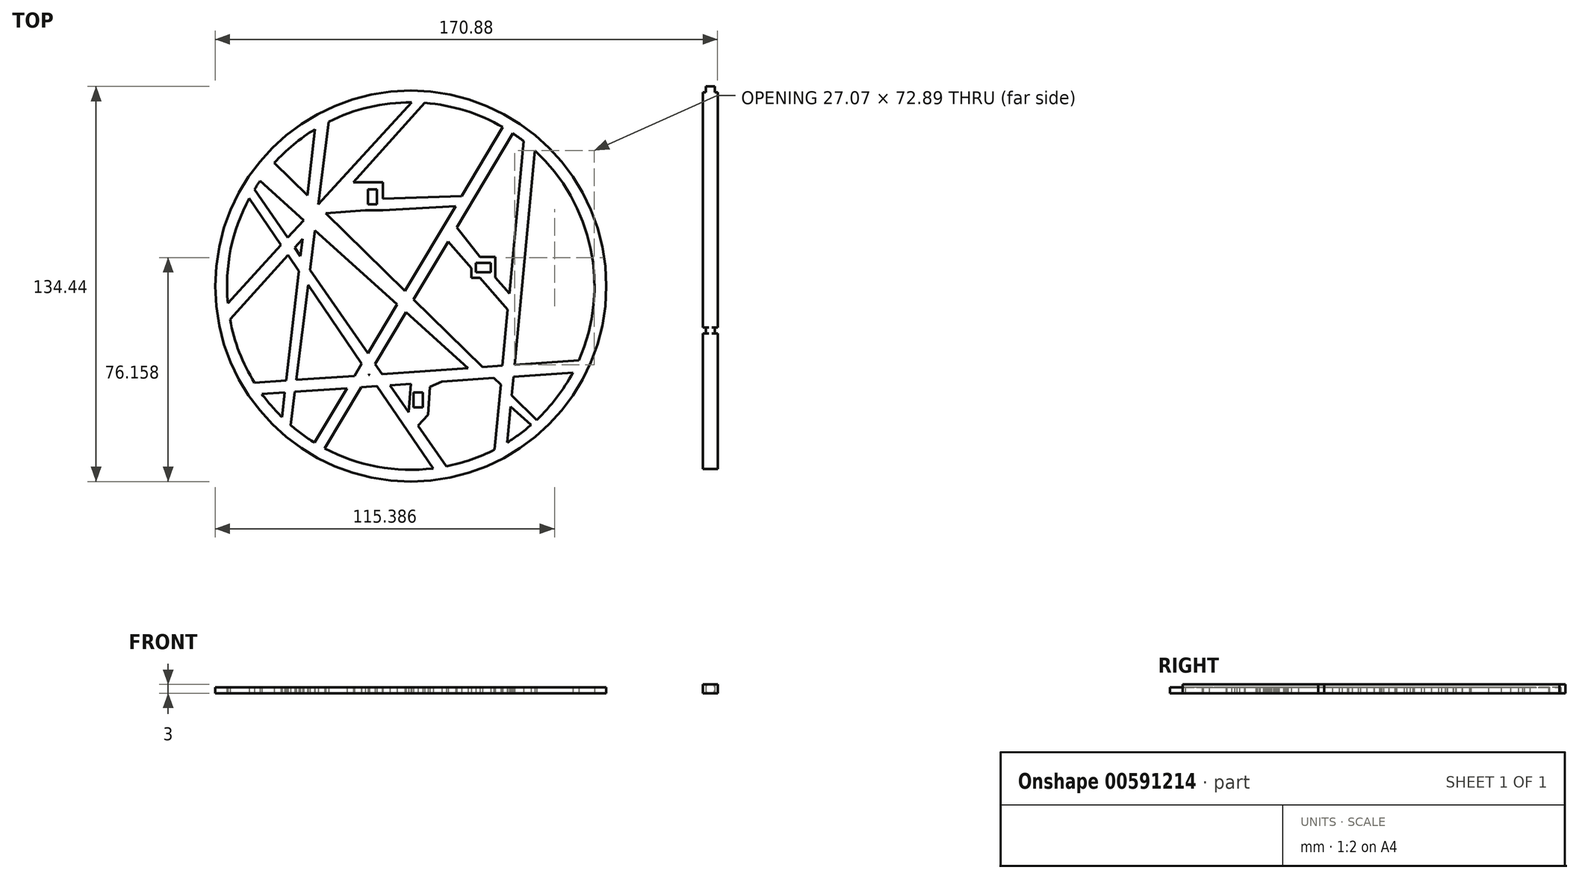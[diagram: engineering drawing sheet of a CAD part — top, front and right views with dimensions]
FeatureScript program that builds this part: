
annotation { "Feature Type Name" : "Feature", "Feature Type Description" : "" }
export const myFeature = defineFeature(function(context is Context, id is Id, definition is map)
    precondition{}
    {
        {
            var Q0;
            Q0=qCreatedBy(makeId("Top.planeOp"),FACE);
            var sketch = newSketch(context, id + "F0", { "sketchPlane" : qUnion([Q0])});
            skCircle(sketch, "E0", {"center": v(0, 0) * mm, "radius": 66.5 * mm});
            skArc(sketch, "E1.0", {"start": v(38.38, 49.32) * mm, "mid": v(36.59, 50.67) * mm, "end": v(34.75, 51.95) * mm});
            skLineSegment(sketch, "E2", {"start": v(-54.93, 29.82) * mm, "end": v(-44.14, 13.98) * mm});
            skLineSegment(sketch, "E3", {"start": v(-53.14, -32.9) * mm, "end": v(-42.35, -32.16) * mm});
            skLineSegment(sketch, "E4", {"start": v(-32.73, -53.24) * mm, "end": v(-21.68, -34.74) * mm});
            skLineSegment(sketch, "E5.0", {"start": v(-29.26, -55.23) * mm, "end": v(-16.82, -34.4) * mm});
            skLineSegment(sketch, "E6.0", {"start": v(32.88, -53.15) * mm, "end": v(34.02, -41.03) * mm});
            skLineSegment(sketch, "E7.0", {"start": v(-50.56, -36.74) * mm, "end": v(-42.82, -36.2) * mm});
            skLineSegment(sketch, "E8.trimOffspring", {"start": v(45.68, -48.33) * mm, "end": v(34.37, -37.25) * mm});
            skLineSegment(sketch, "E9.trimOffspring", {"start": v(40.92, -47.25) * mm, "end": v(34.02, -41.03) * mm});
            skLineSegment(sketch, "E10.trimOffspring", {"start": v(28.53, -55.6) * mm, "end": v(30.6, -33.56) * mm});
            skLineSegment(sketch, "E11.trimOffspring", {"start": v(-53.17, 32.85) * mm, "end": v(-41.84, 16.49) * mm});
            skLineSegment(sketch, "E12.trimOffspring", {"start": v(-32.53, 53.37) * mm, "end": v(-35.12, 30.81) * mm});
            skLineSegment(sketch, "E13.trimOffspring", {"start": v(-27.92, 55.92) * mm, "end": v(-31.43, 27.86) * mm});
            skLineSegment(sketch, "E14.trimOffspring", {"start": v(0.28, 62.5) * mm, "end": v(-31.43, 27.86) * mm});
            skArc(sketch, "E15.trimOffspring", {"start": v(31.35, 54.07) * mm, "mid": v(18.54, 59.69) * mm, "end": v(4.8, 62.32) * mm});
            skLineSegment(sketch, "E16.trimOffspring", {"start": v(4.8, 62.32) * mm, "end": v(-19.45, 35.37) * mm});
            skArc(sketch, "E17.trimOffspring", {"start": v(0.28, 62.5) * mm, "mid": v(-14.2, 60.86) * mm, "end": v(-27.92, 55.92) * mm});
            skArc(sketch, "E18.trimOffspring", {"start": v(-32.53, 53.37) * mm, "mid": v(-39.88, 48.12) * mm, "end": v(-46.4, 41.87) * mm});
            skArc(sketch, "E19.trimOffspring", {"start": v(-51.24, 35.8) * mm, "mid": v(-52.23, 34.33) * mm, "end": v(-53.17, 32.85) * mm});
            skArc(sketch, "E20.trimOffspring", {"start": v(-54.93, 29.82) * mm, "mid": v(-61.23, 12.56) * mm, "end": v(-62.23, -5.79) * mm});
            skArc(sketch, "E21.trimOffspring", {"start": v(-61.47, -11.32) * mm, "mid": v(-58.3, -22.5) * mm, "end": v(-53.14, -32.9) * mm});
            skArc(sketch, "E22.trimOffspring", {"start": v(-50.56, -36.74) * mm, "mid": v(-47.34, -40.81) * mm, "end": v(-43.78, -44.6) * mm});
            skLineSegment(sketch, "E23.trimOffspring", {"start": v(-42.82, -36.2) * mm, "end": v(-43.78, -44.6) * mm});
            skLineSegment(sketch, "E24.trimOffspring", {"start": v(-39.42, -35.97) * mm, "end": v(-40.84, -47.31) * mm});
            skLineSegment(sketch, "E25.trimOffspring", {"start": v(-38.91, -31.92) * mm, "end": v(-19.19, -30.56) * mm});
            skLineSegment(sketch, "E26.trimOffspring", {"start": v(-39.42, -35.97) * mm, "end": v(-21.68, -34.74) * mm});
            skArc(sketch, "E27.trimOffspring", {"start": v(-40.84, -47.31) * mm, "mid": v(-36.9, -50.44) * mm, "end": v(-32.73, -53.24) * mm});
            skArc(sketch, "E28.trimOffspring", {"start": v(-29.26, -55.23) * mm, "mid": v(-0.41, -62.5) * mm, "end": v(28.53, -55.6) * mm});
            skArc(sketch, "E29.trimOffspring", {"start": v(32.88, -53.15) * mm, "mid": v(37.01, -50.36) * mm, "end": v(40.92, -47.25) * mm});
            skLineSegment(sketch, "E30.trimOffspring", {"start": v(19.43, -27.89) * mm, "end": v(-1.6, -8.93) * mm});
            skArc(sketch, "E31.trimOffspring", {"start": v(42.82, -45.53) * mm, "mid": v(62.5, 0.42) * mm, "end": v(42.2, 46.1) * mm});
            skLineSegment(sketch, "E32.trimOffspring", {"start": v(34.37, -37.25) * mm, "end": v(34.97, -30.82) * mm});
            skLineSegment(sketch, "E33.trimOffspring", {"start": v(30.6, -33.56) * mm, "end": v(28.28, -31.29) * mm});
            skLineSegment(sketch, "E34.trimOffspring", {"start": v(34.97, -30.82) * mm, "end": v(55.14, -29.43) * mm});
            skLineSegment(sketch, "E35.trimOffspring", {"start": v(31.2, -27.07) * mm, "end": v(33, -8.01) * mm});
            skLineSegment(sketch, "E36.trimOffspring", {"start": v(24.45, -27.54) * mm, "end": v(1, -4.56) * mm});
            skLineSegment(sketch, "E37.trimOffspring", {"start": v(35.35, -26.79) * mm, "end": v(57.16, -25.28) * mm});
            skLineSegment(sketch, "E38.trimOffspring", {"start": v(35.35, -26.79) * mm, "end": v(42.2, 46.1) * mm});
            skLineSegment(sketch, "E39.trimOffspring", {"start": v(24.45, -27.54) * mm, "end": v(31.2, -27.07) * mm});
            skLineSegment(sketch, "E40.trimOffspring", {"start": v(1, -4.56) * mm, "end": v(12.79, 15.18) * mm});
            skLineSegment(sketch, "E41.trimOffspring", {"start": v(-1.94, -1.69) * mm, "end": v(15.27, 27.14) * mm});
            skLineSegment(sketch, "E42.trimOffspring", {"start": v(-1.94, -1.69) * mm, "end": v(-28.97, 24.79) * mm});
            skLineSegment(sketch, "E43.trimOffspring", {"start": v(-4.64, -6.2) * mm, "end": v(-32.54, 18.95) * mm});
            skLineSegment(sketch, "E44.trimOffspring", {"start": v(-44.14, 13.98) * mm, "end": v(-62.23, -5.79) * mm});
            skLineSegment(sketch, "E45.trimOffspring", {"start": v(-39.5, 13.1) * mm, "end": v(-37.49, 10.2) * mm});
            skLineSegment(sketch, "E46.trimOffspring", {"start": v(-41.8, 10.54) * mm, "end": v(-61.47, -11.32) * mm});
            skLineSegment(sketch, "E47.trimOffspring", {"start": v(-41.8, 10.54) * mm, "end": v(-38.08, 5.07) * mm});
            skLineSegment(sketch, "E48.trimOffspring", {"start": v(-11.45, -34.03) * mm, "end": v(7.62, -62.03) * mm});
            skLineSegment(sketch, "E49.trimOffspring", {"start": v(-14.33, -30.22) * mm, "end": v(-14.2, -30) * mm});
            skLineSegment(sketch, "E50.trimOffspring", {"start": v(-14.33, -30.22) * mm, "end": v(-14.06, -30.2) * mm});
            skLineSegment(sketch, "E51.trimOffspring", {"start": v(-14.2, -30) * mm, "end": v(-14.06, -30.2) * mm});
            skLineSegment(sketch, "E52.trimOffspring", {"start": v(-12.09, -26.47) * mm, "end": v(-1.6, -8.93) * mm});
            skLineSegment(sketch, "E53.trimOffspring", {"start": v(-9.7, -29.9) * mm, "end": v(19.43, -27.89) * mm});
            skLineSegment(sketch, "E54.trimOffspring", {"start": v(-14.59, -22.86) * mm, "end": v(-4.64, -6.2) * mm});
            skLineSegment(sketch, "E55.trimOffspring", {"start": v(-12.09, -26.47) * mm, "end": v(-9.7, -29.9) * mm});
            skLineSegment(sketch, "E56.trimOffspring", {"start": v(-7.06, -33.73) * mm, "end": v(-0.67, -42.95) * mm});
            skLineSegment(sketch, "E57.trimOffspring", {"start": v(-7.06, -33.73) * mm, "end": v(0, -33.24) * mm});
            skLineSegment(sketch, "E58.trimOffspring", {"start": v(-16.82, -34.4) * mm, "end": v(-11.45, -34.03) * mm});
            skLineSegment(sketch, "E59.trimOffspring", {"start": v(-19.19, -30.56) * mm, "end": v(-16.68, -26.36) * mm});
            skLineSegment(sketch, "E60.trimOffspring", {"start": v(-34.87, 0.36) * mm, "end": v(-38.91, -31.92) * mm});
            skLineSegment(sketch, "E61.trimOffspring", {"start": v(-34.87, 0.36) * mm, "end": v(-16.68, -26.36) * mm});
            skLineSegment(sketch, "E62.trimOffspring", {"start": v(-38.08, 5.07) * mm, "end": v(-42.35, -32.16) * mm});
            skLineSegment(sketch, "E63.trimOffspring", {"start": v(-34.23, 5.5) * mm, "end": v(-14.59, -22.86) * mm});
            skLineSegment(sketch, "E64.trimOffspring", {"start": v(-36.81, 16.07) * mm, "end": v(-39.5, 13.1) * mm});
            skLineSegment(sketch, "E65.trimOffspring", {"start": v(-36.81, 16.07) * mm, "end": v(-37.49, 10.2) * mm});
            skLineSegment(sketch, "E66.trimOffspring", {"start": v(-36.11, 22.17) * mm, "end": v(-51.24, 35.8) * mm});
            skLineSegment(sketch, "E67.trimOffspring", {"start": v(-32.54, 18.95) * mm, "end": v(-34.23, 5.5) * mm});
            skLineSegment(sketch, "E68.trimOffspring", {"start": v(-36.04, 22.83) * mm, "end": v(-41.84, 16.49) * mm});
            skLineSegment(sketch, "E69.trimOffspring", {"start": v(-35.12, 30.81) * mm, "end": v(-46.4, 41.87) * mm});
            skLineSegment(sketch, "E70.left", {"start": v(0, -33.24) * mm, "end": v(-0.67, -42.95) * mm});
            skLineSegment(sketch, "E70.right", {"start": v(6.54, -34.25) * mm, "end": v(5.89, -43.75) * mm});
            skLineSegment(sketch, "E71", {"start": v(6.54, -34.25) * mm, "end": v(10.6, -32.5) * mm});
            skLineSegment(sketch, "E72.trimOffspring", {"start": v(10.6, -32.5) * mm, "end": v(28.28, -31.29) * mm});
            skLineSegment(sketch, "E73.top", {"start": v(0.96, -41.22) * mm, "end": v(4.06, -41.22) * mm});
            skLineSegment(sketch, "E73.left", {"start": v(0.96, -37.12) * mm, "end": v(0.96, -41.22) * mm});
            skLineSegment(sketch, "E73.right", {"start": v(4.06, -37.12) * mm, "end": v(4.06, -41.22) * mm});
            skLineSegment(sketch, "E74.bottom", {"start": v(-19.45, 35.37) * mm, "end": v(-9.5, 35.37) * mm});
            skLineSegment(sketch, "E74.top", {"start": v(-15.5, 25.78) * mm, "end": v(-9.5, 25.78) * mm});
            skLineSegment(sketch, "E74.right", {"start": v(-9.5, 35.37) * mm, "end": v(-9.5, 29.78) * mm});
            skLineSegment(sketch, "E75", {"start": v(-9.5, 25.78) * mm, "end": v(15.27, 27.14) * mm});
            skPoint(sketch, "E76.endSnap0", {"position": v(-9.5, 30.57) * mm});
            skLineSegment(sketch, "E77", {"start": v(17.32, 30.57) * mm, "end": v(-9.5, 29.78) * mm});
            skLineSegment(sketch, "E78", {"start": v(-15.5, 25.78) * mm, "end": v(-28.97, 24.79) * mm});
            skLineSegment(sketch, "E79.top", {"start": v(-14.6, 27.78) * mm, "end": v(-11.5, 27.78) * mm});
            skLineSegment(sketch, "E79.left", {"start": v(-14.6, 31.88) * mm, "end": v(-14.6, 27.78) * mm});
            skLineSegment(sketch, "E79.right", {"start": v(-11.5, 31.88) * mm, "end": v(-11.5, 27.78) * mm});
            skLineSegment(sketch, "E80.bottom", {"start": v(23.59, 9.87) * mm, "end": v(28.77, 9.87) * mm});
            skLineSegment(sketch, "E80.top", {"start": v(20.67, 2.77) * mm, "end": v(23.6, 2.77) * mm});
            skLineSegment(sketch, "E80.left", {"start": v(20.67, 6.13) * mm, "end": v(20.67, 2.77) * mm});
            skLineSegment(sketch, "E80.right", {"start": v(28.77, 9.87) * mm, "end": v(28.77, 2.77) * mm});
            skLineSegment(sketch, "E81.1", {"start": v(22.67, 7.87) * mm, "end": v(26.77, 7.87) * mm});
            skLineSegment(sketch, "E81.3", {"start": v(22.67, 4.77) * mm, "end": v(26.77, 4.77) * mm});
            skLineSegment(sketch, "E82", {"start": v(33, -8.01) * mm, "end": v(23.6, 2.77) * mm});
            skLineSegment(sketch, "E83.0", {"start": v(33.51, -2.52) * mm, "end": v(28.77, 2.93) * mm});
            skLineSegment(sketch, "E84.trimOffspring", {"start": v(20.67, 6.13) * mm, "end": v(12.79, 15.18) * mm});
            skLineSegment(sketch, "E85.trimOffspring", {"start": v(23.59, 9.87) * mm, "end": v(15.68, 20.02) * mm});
            skLineSegment(sketch, "E86.trimOffspring", {"start": v(33.51, -2.52) * mm, "end": v(38.38, 49.32) * mm});
            skLineSegment(sketch, "E87.trimOffspring", {"start": v(15.68, 20.02) * mm, "end": v(34.75, 51.95) * mm});
            skLineSegment(sketch, "E88.trimOffspring", {"start": v(17.32, 30.57) * mm, "end": v(31.35, 54.07) * mm});
            skLineSegment(sketch, "E89", {"start": v(5.89, -43.75) * mm, "end": v(2.5, -47.53) * mm});
            skLineSegment(sketch, "E90.trimOffspring", {"start": v(2.5, -47.53) * mm, "end": v(12.06, -61.33) * mm});
            skLineSegment(sketch, "E91.0", {"start": v(27.27, 7.87) * mm, "end": v(27.27, 4.77) * mm});
            skLineSegment(sketch, "E92.0", {"start": v(22.17, 7.87) * mm, "end": v(22.17, 4.77) * mm});
            skLineSegment(sketch, "E93.0", {"start": v(-14.6, 32.88) * mm, "end": v(-11.5, 32.88) * mm});
            skLineSegment(sketch, "E94.0", {"start": v(0.96, -36.12) * mm, "end": v(4.06, -36.12) * mm});
            skLineSegment(sketch, "E95", {"start": v(-14.6, 32.88) * mm, "end": v(-14.6, 31.88) * mm});
            skLineSegment(sketch, "E96", {"start": v(-11.5, 32.88) * mm, "end": v(-11.5, 31.88) * mm});
            skLineSegment(sketch, "E97", {"start": v(22.17, 7.87) * mm, "end": v(22.67, 7.87) * mm});
            skLineSegment(sketch, "E98", {"start": v(26.77, 7.87) * mm, "end": v(27.27, 7.87) * mm});
            skLineSegment(sketch, "E99", {"start": v(27.27, 4.77) * mm, "end": v(26.77, 4.77) * mm});
            skLineSegment(sketch, "E100", {"start": v(22.17, 4.77) * mm, "end": v(22.67, 4.77) * mm});
            skLineSegment(sketch, "E101", {"start": v(0.96, -37.12) * mm, "end": v(0.96, -36.12) * mm});
            skLineSegment(sketch, "E102", {"start": v(4.06, -36.12) * mm, "end": v(4.06, -37.12) * mm});
            skSolve(sketch);
        }
        {
            var Q0;
            Q0=makeQuery(id+"F0.imprint","IMPRINT",FACE,{"disambiguationData":[TD([[makeQuery(id+"F0.imprint","IMPRINT",EDGE,{"derivedFrom":sQuery(id+"F0.wireOp",EDGE,"E0")}),1.0]])]});
            extrude(context, id + "F1", {"entities" : qUnion([Q0]), "depth" : 2 * mm, "offsetDistance" : 25 * mm});
        }
        {
            var Q0;
            Q0=qCreatedBy(makeId("Top.planeOp"),FACE);
            var sketch = newSketch(context, id + "F2", { "sketchPlane" : qUnion([Q0])});
            skLineSegment(sketch, "E103.bottom", {"start": v(100.38, 67.94) * mm, "end": v(103.38, 67.94) * mm});
            skLineSegment(sketch, "E103.top", {"start": v(100.38, -62.16) * mm, "end": v(103.38, -62.16) * mm});
            skLineSegment(sketch, "E103.left", {"start": v(100.38, 67.94) * mm, "end": v(100.38, 65.94) * mm});
            skLineSegment(sketch, "E103.right", {"start": v(103.38, 67.94) * mm, "end": v(103.38, 65.94) * mm});
            skLineSegment(sketch, "E104.bottom", {"start": v(99.38, 65.94) * mm, "end": v(100.38, 65.94) * mm});
            skLineSegment(sketch, "E104.top", {"start": v(99.38, -62.16) * mm, "end": v(104.38, -62.16) * mm});
            skLineSegment(sketch, "E104.left", {"start": v(99.38, 65.94) * mm, "end": v(99.38, -14.06) * mm});
            skLineSegment(sketch, "E104.right", {"start": v(104.38, 65.94) * mm, "end": v(104.38, -14.06) * mm});
            skLineSegment(sketch, "E105", {"start": v(99.38, -16.16) * mm, "end": v(100.38, -16.16) * mm});
            skLineSegment(sketch, "E106", {"start": v(104.38, -14.06) * mm, "end": v(103.38, -14.06) * mm});
            skLineSegment(sketch, "E107.trimOffspring", {"start": v(104.38, -16.16) * mm, "end": v(104.38, -62.16) * mm});
            skLineSegment(sketch, "E108.trimOffspring", {"start": v(99.38, -16.16) * mm, "end": v(99.38, -62.16) * mm});
            skLineSegment(sketch, "E109.trimOffspring", {"start": v(100.38, -14.06) * mm, "end": v(99.38, -14.06) * mm});
            skLineSegment(sketch, "E110.trimOffspring", {"start": v(103.38, -16.16) * mm, "end": v(104.38, -16.16) * mm});
            skLineSegment(sketch, "E111.trimOffspring", {"start": v(103.38, -14.06) * mm, "end": v(103.38, -16.16) * mm});
            skLineSegment(sketch, "E112.trimOffspring", {"start": v(100.38, -14.06) * mm, "end": v(100.38, -16.16) * mm});
            skLineSegment(sketch, "E113.trimOffspring", {"start": v(103.38, 65.94) * mm, "end": v(104.38, 65.94) * mm});
            skSolve(sketch);
        }
        {
            var Q0;
            Q0=makeQuery(id+"F2.imprint","IMPRINT",FACE,{"disambiguationData":[TD([[makeQuery(id+"F2.imprint","IMPRINT",EDGE,{"derivedFrom":sQuery(id+"F2.wireOp",EDGE,"E103.bottom")}),-1.0]])]});
            extrude(context, id + "F3", {"entities" : qUnion([Q0]), "depth" : 3 * mm, "offsetDistance" : 25 * mm});
        }
        {
            var Q0;
            Q0=makeQuery(id+"F3.opExtrude","CAP_EDGE",EDGE,{"disambiguationData":[OSD([sQuery(id+"F2.wireOp",EDGE,"E111.trimOffspring")])],"isStart":false});
            var Q1;
            Q1=makeQuery(id+"F3.opExtrude","CAP_EDGE",EDGE,{"disambiguationData":[OSD([sQuery(id+"F2.wireOp",EDGE,"E112.trimOffspring")])],"isStart":false});
            var Q2;
            Q2=makeQuery(id+"F3.opExtrude","CAP_EDGE",EDGE,{"disambiguationData":[OSD([sQuery(id+"F2.wireOp",EDGE,"E111.trimOffspring")])],"isStart":true});
            var Q3;
            Q3=makeQuery(id+"F3.opExtrude","CAP_EDGE",EDGE,{"disambiguationData":[OSD([sQuery(id+"F2.wireOp",EDGE,"E112.trimOffspring")])],"isStart":true});
            fillet(context, id + "F4", {"entities" : qUnion([Q0, Q1, Q2, Q3]), "radius" : 1 * mm, "tangentPropagation" : true, "allowEdgeOverflow" : false});
        }
    });
